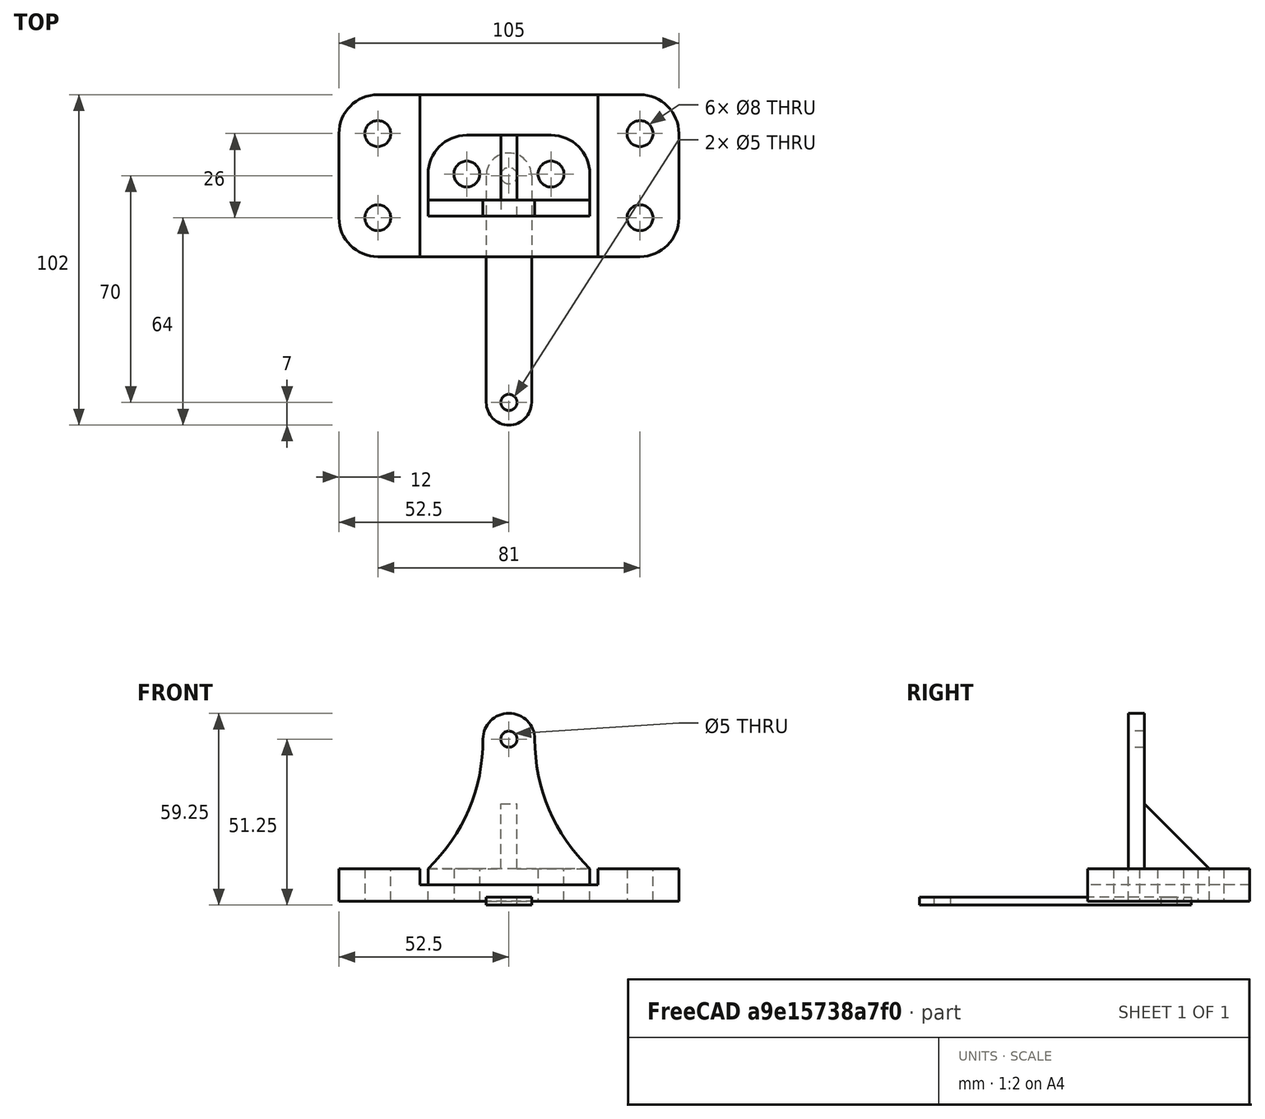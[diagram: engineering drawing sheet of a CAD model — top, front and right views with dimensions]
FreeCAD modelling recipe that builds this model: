
FCSTD DOCUMENT  (FreeCAD 1.0R39319 (Git))
Label: Assignment_7.1_Base
License: All rights reserved
LicenseURL: https://en.wikipedia.org/wiki/All_rights_reserved
objects: TechDraw::DrawViewDimension×15, Sketcher::SketchObject×7, PartDesign::Pad×5, TechDraw::DrawProjGroupItem×4, TechDraw::DrawViewAnnotation×4, PartDesign::Body×3, TechDraw::DrawViewBalloon×3, PartDesign::Pocket×1, TechDraw::DrawSVGTemplate×1, TechDraw::DrawProjGroup×1, TechDraw::DrawPage×1
note: 58 computed .brp shape members not serialized (recipe doc carries the construction recipe); baked Part::Feature solids carry a one-line shape summary decoded from their .brp

FEATURE [Sketcher::SketchObject] Sketch
  ArcFitTolerance = 1e-06
  AttachmentSupport = -> [XY_Plane]
  FullyConstrained = true
  MakeInternals = false
  MapMode = 5
  sketch-geometry (14):
    g0: LineSegment StartX=-52.5 StartY=13 StartZ=0 EndX=-52.5 EndY=-13 EndZ=0
    g1: LineSegment StartX=-40.5 StartY=-25 StartZ=0 EndX=40.5 EndY=-25 EndZ=0
    g2: LineSegment StartX=52.5 StartY=-13 StartZ=0 EndX=52.5 EndY=13 EndZ=0
    g3: LineSegment StartX=40.5 StartY=25 StartZ=0 EndX=-40.5 EndY=25 EndZ=0
    g4: ArcOfCircle CenterX=-40.5 CenterY=13 CenterZ=0 NormalX=0 NormalY=0 NormalZ=1 AngleXU=0 Radius=12 StartAngle=1.5708 EndAngle=3.14159
    g5: ArcOfCircle CenterX=-40.5 CenterY=-13 CenterZ=0 NormalX=0 NormalY=0 NormalZ=1 AngleXU=0 Radius=12 StartAngle=3.14159 EndAngle=4.71239
    g6: ArcOfCircle CenterX=40.5 CenterY=-13 CenterZ=0 NormalX=0 NormalY=0 NormalZ=1 AngleXU=0 Radius=12 StartAngle=4.71239 EndAngle=6.28319
    g7: ArcOfCircle CenterX=40.5 CenterY=13 CenterZ=0 NormalX=0 NormalY=0 NormalZ=1 AngleXU=0 Radius=12 StartAngle=0 EndAngle=1.5708
    g8: GeomPoint [constr] X=-52.5 Y=25 Z=0
    g9: GeomPoint [constr] X=52.5 Y=-25 Z=0
    g10: Circle CenterX=-40.5 CenterY=13 CenterZ=0 NormalX=0 NormalY=0 NormalZ=1 AngleXU=0 Radius=4
    g11: Circle CenterX=40.5 CenterY=13 CenterZ=0 NormalX=0 NormalY=0 NormalZ=1 AngleXU=0 Radius=4
    g12: Circle CenterX=40.5 CenterY=-13 CenterZ=0 NormalX=0 NormalY=0 NormalZ=1 AngleXU=0 Radius=4
    g13: Circle CenterX=-40.5 CenterY=-13 CenterZ=0 NormalX=0 NormalY=0 NormalZ=1 AngleXU=0 Radius=4
  constraints (31):
    c: Tangent(g0,g4) = -1.5708
    c: Tangent(g0,g5) = -1.5708
    c: Tangent(g1,g5) = -1.5708
    c: Tangent(g1,g6) = -1.5708
    c: Tangent(g2,g6) = -1.5708
    c: Tangent(g2,g7) = -1.5708
    c: Tangent(g3,g7) = -1.5708
    c: Tangent(g3,g4) = -1.5708
    c: Vertical(g0)
    c: Vertical(g2)
    c: Horizontal(g1)
    c: Horizontal(g3)
    c: Equal(g4,g5)
    c: Equal(g5,g6)
    c: Equal(g6,g7)
    c: PointOnObject(g8,g0)
    c: PointOnObject(g8,g3)
    c: PointOnObject(g9,g1)
    c: PointOnObject(g9,g2)
    c: Symmetric(g4,g6,g-1)
    c: Distance(g2,g0) = 105
    c: Distance(g1,g3) = 50
    c: Radius(g4) = 12
    c: Coincident(g10,g4)
    c: Coincident(g11,g7)
    c: Coincident(g12,g6)
    c: Coincident(g13,g5)
    c: Equal(g10,g11)
    c: Equal(g10,g12)
    c: Equal(g10,g13)
    c: Diameter(g10) = 8
FEATURE [PartDesign::Pad] Pad
  Direction = (0,0,1)
  Length = 10
  Length2 = 10
  Profile = -> Sketch
  ReferenceAxis = -> Sketch [N_Axis]
  Refine = true
  Suppressed = false
  Type = 0
FEATURE [Sketcher::SketchObject] Sketch001
  ArcFitTolerance = 1e-06
  AttachmentSupport = -> [Pad]
  ExternalGeometry = -> [Pad]
  FullyConstrained = true
  MakeInternals = false
  MapMode = 5
  Placement = pos=(0,0,10) rot=(0,0,1;0rad)
  sketch-geometry (5):
    g0: LineSegment StartX=27.5 StartY=-25 StartZ=0 EndX=27.5 EndY=25 EndZ=0
    g1: LineSegment StartX=27.5 StartY=25 StartZ=0 EndX=-27.5 EndY=25 EndZ=0
    g2: LineSegment StartX=-27.5 StartY=25 StartZ=0 EndX=-27.5 EndY=-25 EndZ=0
    g3: LineSegment StartX=-27.5 StartY=-25 StartZ=0 EndX=27.5 EndY=-25 EndZ=0
    g4: GeomPoint [constr] X=0 Y=0 Z=0
  constraints (12):
    c: Coincident(g0,g1)
    c: Coincident(g1,g2)
    c: Coincident(g2,g3)
    c: Coincident(g3,g0)
    c: Vertical(g0)
    c: Vertical(g2)
    c: Horizontal(g1)
    c: Horizontal(g3)
    c: Symmetric(g2,g0,g4)
    c: Coincident(g4,g-1)
    c: PointOnObject(g1,g-3)
    c: Distance(g0,g2) = 55
FEATURE [PartDesign::Pocket] Pocket
  BaseFeature = -> Pad
  Direction = (0,0,-1)
  Length = 5
  Length2 = 5
  Profile = -> Sketch001
  ReferenceAxis = -> Sketch001 [N_Axis]
  Refine = true
  Suppressed = false
  Type = 0
FEATURE [PartDesign::Body] Body  label="Base"
  AllowCompound = false
  Group = -> [Sketch,Pad,Sketch001,Pocket]
  Origin = -> Origin
  Tip = -> Pocket
FEATURE [Sketcher::SketchObject] Sketch002
  ArcFitTolerance = 1e-06
  AttachmentSupport = -> [XY_Plane001]
  FullyConstrained = true
  MakeInternals = false
  MapMode = 5
  sketch-geometry (11):
    g0: LineSegment StartX=-25 StartY=-12.5 StartZ=0 EndX=25 EndY=-12.5 EndZ=0
    g1: LineSegment StartX=25 StartY=-12.5 StartZ=0 EndX=25 EndY=0.5 EndZ=0
    g2: LineSegment StartX=13 StartY=12.5 StartZ=0 EndX=-13 EndY=12.5 EndZ=0
    g3: LineSegment StartX=-25 StartY=0.5 StartZ=0 EndX=-25 EndY=-12.5 EndZ=0
    g4: GeomPoint [constr] X=0 Y=0 Z=0
    g5: ArcOfCircle CenterX=-13 CenterY=0.5 CenterZ=0 NormalX=0 NormalY=0 NormalZ=1 AngleXU=0 Radius=12 StartAngle=1.5708 EndAngle=3.14159
    g6: GeomPoint [constr] X=-25 Y=12.5 Z=0
    g7: ArcOfCircle CenterX=13 CenterY=0.5 CenterZ=0 NormalX=0 NormalY=0 NormalZ=1 AngleXU=0 Radius=12 StartAngle=0 EndAngle=1.5708
    g8: GeomPoint [constr] X=25 Y=12.5 Z=0
    g9: Circle CenterX=13 CenterY=0.5 CenterZ=0 NormalX=0 NormalY=0 NormalZ=1 AngleXU=0 Radius=4
    g10: Circle CenterX=-13 CenterY=0.5 CenterZ=0 NormalX=0 NormalY=0 NormalZ=1 AngleXU=0 Radius=4
  constraints (24):
    c: Coincident(g0,g1)
    c: Coincident(g3,g0)
    c: Horizontal(g0)
    c: Horizontal(g2)
    c: Vertical(g1)
    c: Vertical(g3)
    c: Symmetric(g8,g0,g4)
    c: Distance(g1,g3) = 50
    c: Distance(g0,g6) = 25
    c: Coincident(g4,g-1)
    c: PointOnObject(g6,g3)
    c: PointOnObject(g6,g2)
    c: Tangent(g3,g5) = -1.5708
    c: Tangent(g2,g5) = -1.5708
    c: PointOnObject(g8,g1)
    c: PointOnObject(g8,g2)
    c: Tangent(g1,g7) = -1.5708
    c: Tangent(g2,g7) = -1.5708
    c: Equal(g5,g7)
    c: Radius(g5) = 12
    c: Coincident(g9,g7)
    c: Coincident(g10,g5)
    c: Equal(g10,g9)
    c: Diameter(g10) = 8
FEATURE [PartDesign::Pad] Pad001
  Direction = (0,0,1)
  Length = 10
  Length2 = 10
  Profile = -> Sketch002
  ReferenceAxis = -> Sketch002 [N_Axis]
  Refine = true
  Suppressed = false
  Type = 0
FEATURE [Sketcher::SketchObject] Sketch003
  ArcFitTolerance = 1e-06
  AttachmentSupport = -> [Pad001]
  FullyConstrained = true
  MakeInternals = false
  MapMode = 5
  Placement = pos=(0,-12.5,0) rot=(1,0,0;1.5708rad)
FEATURE [Sketcher::SketchObject] Sketch004
  ArcFitTolerance = 1e-06
  AttachmentSupport = -> [Pad001]
  ExternalGeometry = -> [Pad001]
  FullyConstrained = true
  MakeInternals = false
  MapMode = 5
  Placement = pos=(0,-12.5,0) rot=(1,0,0;1.5708rad)
  sketch-geometry (5):
    g0: ArcOfCircle CenterX=-63.5588 CenterY=50 CenterZ=0 NormalX=0 NormalY=0 NormalZ=1 AngleXU=0 Radius=55.5588 StartAngle=5.47944 EndAngle=6.28319
    g1: ArcOfCircle CenterX=0 CenterY=50 CenterZ=0 NormalX=0 NormalY=0 NormalZ=1 AngleXU=0 Radius=8 StartAngle=0 EndAngle=3.14159
    g2: ArcOfCircle CenterX=63.5588 CenterY=50 CenterZ=0 NormalX=0 NormalY=0 NormalZ=1 AngleXU=0 Radius=55.5588 StartAngle=3.14159 EndAngle=3.94533
    g3: Circle CenterX=0 CenterY=50 CenterZ=0 NormalX=0 NormalY=0 NormalZ=1 AngleXU=0 Radius=2.5
    g4: LineSegment StartX=-25 StartY=10 StartZ=0 EndX=25 EndY=10 EndZ=0
  constraints (13):
    c: Tangent(g0,g1) = 1.5708
    c: Tangent(g1,g2) = 1.5708
    c: Coincident(g2,g-4)
    c: Coincident(g0,g-5)
    c: PointOnObject(g1,g-2)
    c: Equal(g0,g2)
    c: Radius(g1) = 8
    c: Coincident(g3,g1)
    c: Diameter(g3) = 5
    c: Horizontal(g0,g1)
    c: DistanceY(g-1,g1) = 50
    c: Coincident(g4,g0)
    c: Coincident(g4,g2)
FEATURE [PartDesign::Pad] Pad002
  BaseFeature = -> Pad001
  Direction = (0,-1,2e-16)
  Length = 5
  Length2 = 10
  Profile = -> Sketch004
  ReferenceAxis = -> Sketch004 [N_Axis]
  Refine = true
  Reversed = true
  Suppressed = false
  Type = 0
FEATURE [Sketcher::SketchObject] Sketch008
  ArcFitTolerance = 1e-06
  AttachmentSupport = -> [YZ_Plane001]
  ExternalGeometry = -> [Pad002]
  FullyConstrained = true
  MakeInternals = false
  MapMode = 5
  Placement = pos=(0,0,0) rot=(0.57735,0.57735,0.57735;2.0944rad)
  sketch-geometry (3):
    g0: LineSegment StartX=-7.5 StartY=10 StartZ=0 EndX=-7.5 EndY=30 EndZ=0
    g1: LineSegment StartX=12.5 StartY=10 StartZ=0 EndX=-7.5 EndY=30 EndZ=0
    g2: LineSegment StartX=12.5 StartY=10 StartZ=0 EndX=-7.5 EndY=10 EndZ=0
  constraints (7):
    c: Coincident(g0,g-3)
    c: PointOnObject(g0,g-3)
    c: Coincident(g1,g-4)
    c: Coincident(g1,g0)
    c: Coincident(g2,g1)
    c: Coincident(g2,g0)
    c: DistanceY(g0,g0) = 20
FEATURE [PartDesign::Pad] Pad004
  BaseFeature = -> Pad002
  Direction = (1,0,0)
  Length = 5
  Length2 = 10
  Midplane = true
  Profile = -> Sketch008
  ReferenceAxis = -> Sketch008 [N_Axis]
  Refine = true
  Suppressed = false
  Type = 0
FEATURE [PartDesign::Body] Body001  label="Bracket"
  AllowCompound = false
  Group = -> [Sketch002,Pad001,Sketch003,Sketch004,Pad002,Sketch008,Pad004]
  Origin = -> Origin001
  Tip = -> Pad004
FEATURE [Sketcher::SketchObject] Sketch009
  ArcFitTolerance = 1e-06
  AttachmentSupport = -> [XY_Plane002]
  FullyConstrained = true
  MakeInternals = false
  MapMode = 5
  sketch-geometry (6):
    g0: ArcOfCircle CenterX=0 CenterY=0 CenterZ=0 NormalX=0 NormalY=0 NormalZ=1 AngleXU=0 Radius=7 StartAngle=1e-16 EndAngle=3.14159
    g1: ArcOfCircle CenterX=2e-16 CenterY=-70 CenterZ=0 NormalX=0 NormalY=0 NormalZ=1 AngleXU=0 Radius=7 StartAngle=3.14159 EndAngle=6.28319
    g2: LineSegment StartX=7 StartY=9e-16 StartZ=0 EndX=7 EndY=-70 EndZ=0
    g3: LineSegment StartX=-7 StartY=0 StartZ=0 EndX=-7 EndY=-70 EndZ=0
    g4: Circle CenterX=0 CenterY=0 CenterZ=0 NormalX=0 NormalY=0 NormalZ=1 AngleXU=0 Radius=2.5
    g5: Circle CenterX=2e-16 CenterY=-70 CenterZ=0 NormalX=0 NormalY=0 NormalZ=1 AngleXU=0 Radius=2.5
  constraints (13):
    c: Tangent(g0,g2) = 1.5708
    c: Tangent(g0,g3) = -1.5708
    c: Tangent(g1,g2) = 1.5708
    c: Tangent(g1,g3) = -1.5708
    c: Equal(g0,g1)
    c: Vertical(g3)
    c: Coincident(g0,g-1)
    c: Coincident(g5,g1)
    c: Equal(g4,g5)
    c: Diameter(g4) = 5
    c: DistanceY(g1,g4) = 70
    c: Coincident(g0,g4)
    c: Radius(g0) = 7
FEATURE [PartDesign::Pad] Pad005
  Direction = (0,0,1)
  Length = 2.5
  Length2 = 10
  Midplane = true
  Profile = -> Sketch009
  ReferenceAxis = -> Sketch009 [N_Axis]
  Refine = true
  Suppressed = false
  Type = 0
FEATURE [PartDesign::Body] Body002  label="Links"
  AllowCompound = false
  Group = -> [Sketch009,Pad005]
  Origin = -> Origin002
  Tip = -> Pad005
FEATURE [TechDraw::DrawSVGTemplate] Template002
  EditableTexts = AuthorName=REHAN K. NADAF; CheckDate=CHECK DATE; CreationDate=29-11-2025; DrawingNumber=NUMBER; FC-Title=Bracket; SheetNumber=3 / 3; Subtitle=Assignment_7.1_Slider_Assembly; SupervisorName=ProBUILD; Weight=WEIGHT; scale=1 : 1
  Height = 297
  Orientation = 1
  Template = C:/Program Files/FreeCAD 1.0/data/Mod/TechDraw/Templates/A3_Landscape_TD.svg
  Width = 420
FEATURE [TechDraw::DrawProjGroupItem] View001  label="Front001"
  CoarseView = false
  Direction = (2e-16,1,0)
  Focus = 100
  HardHidden = true
  IsoCount = 0
  IsoHidden = false
  IsoVisible = false
  LockPosition = true
  Perspective = false
  Rotation = 0
  RotationVector = (1,0,0)
  Scale = 1.5
  ScaleType = 2
  ScrubCount = 1
  SeamHidden = false
  SeamVisible = false
  SmoothHidden = false
  SmoothVisible = true
  Source = -> [Body001]
  Type = 0
  X = 0
  XDirection = (-1,2e-16,0)
  Y = 0
FEATURE [TechDraw::DrawProjGroupItem] ProjItem002  label="Left"
  CoarseView = false
  Direction = (1,-1e-16,0)
  Focus = 100
  HardHidden = true
  IsoCount = 0
  IsoHidden = false
  IsoVisible = false
  LockPosition = false
  Perspective = false
  Rotation = 0
  RotationVector = (1,0,0)
  Scale = 1.5
  ScaleType = 2
  ScrubCount = 1
  SeamHidden = false
  SeamVisible = false
  SmoothHidden = false
  SmoothVisible = true
  Source = -> [Body001]
  Type = 1
  X = -161.206
  XDirection = (1e-16,1,0)
  Y = 0
FEATURE [TechDraw::DrawProjGroupItem] ProjItem  label="FrontTopRight"
  CoarseView = true
  Direction = (-0.57735,0.57735,0.57735)
  Focus = 100
  HardHidden = false
  IsoCount = 0
  IsoHidden = true
  IsoVisible = false
  LockPosition = true
  Perspective = false
  Rotation = 0
  RotationVector = (1,0,0)
  Scale = 1.5
  ScaleType = 2
  ScrubCount = 1
  SeamHidden = false
  SeamVisible = false
  SmoothHidden = false
  SmoothVisible = true
  Source = -> [Body001]
  Type = 7
  X = -271.118
  XDirection = (-0.707107,-0.707107,0)
  Y = 105.092
FEATURE [TechDraw::DrawViewDimension] Dimension
  AngleOverride = false
  Arbitrary = false
  ArbitraryTolerances = false
  BoxCorners = (2) [(-12.5,-29,-1e-07),(12.5,29,1e-07)]
  EqualTolerance = true
  ExtensionAngle = 0
  FormatSpec = %.2w
  FormatSpecOverTolerance = %+.2w
  FormatSpecUnderTolerance = %+.2w
  Inverted = false
  LineAngle = 0
  LockPosition = false
  MeasureType = 1
  OverTolerance = 0
  References2D = -> [ProjItem002]
  Rotation = 0
  ScaleType = 0
  TheoreticalExact = false
  Type = 0
  UnderTolerance = 0
  X = 22.1548
  Y = -11.0669
FEATURE [TechDraw::DrawViewDimension] Dimension004
  AngleOverride = false
  Arbitrary = false
  ArbitraryTolerances = false
  BoxCorners = (2) [(-25,-29,-1e-07),(25,29,1e-07)]
  EqualTolerance = true
  ExtensionAngle = 0
  FormatSpec = R%.2w
  FormatSpecOverTolerance = %+.2w
  FormatSpecUnderTolerance = %+.2w
  Inverted = false
  LineAngle = 0
  LockPosition = false
  MeasureType = 1
  OverTolerance = 0
  References2D = -> [View001]
  Rotation = 0
  ScaleType = 0
  TheoreticalExact = false
  Type = 4
  UnderTolerance = 0
  X = 33.9135
  Y = 48.0796
FEATURE [TechDraw::DrawViewDimension] Dimension005
  AngleOverride = false
  Arbitrary = false
  ArbitraryTolerances = false
  BoxCorners = (2) [(-25,-29,-1e-07),(25,29,1e-07)]
  EqualTolerance = true
  ExtensionAngle = 0
  FormatSpec = ⌀%.2w
  FormatSpecOverTolerance = %+.2w
  FormatSpecUnderTolerance = %+.2w
  Inverted = false
  LineAngle = 0
  LockPosition = false
  MeasureType = 1
  OverTolerance = 0
  References2D = -> [View001]
  Rotation = 0
  ScaleType = 0
  TheoreticalExact = false
  Type = 5
  UnderTolerance = 0
  X = 37.2148
  Y = 31.4331
FEATURE [TechDraw::DrawViewDimension] Dimension006
  AngleOverride = false
  Arbitrary = false
  ArbitraryTolerances = false
  BoxCorners = (2) [(-25,-29,-1e-07),(25,29,1e-07)]
  EqualTolerance = true
  ExtensionAngle = 0
  FormatSpec = R%.2w
  FormatSpecOverTolerance = %+.2w
  FormatSpecUnderTolerance = %+.2w
  Inverted = false
  LineAngle = 0
  LockPosition = false
  MeasureType = 1
  OverTolerance = 0
  References2D = -> [View001]
  Rotation = 0
  ScaleType = 0
  TheoreticalExact = false
  Type = 4
  UnderTolerance = 0
  X = -54.0533
  Y = 26.8958
FEATURE [TechDraw::DrawViewDimension] Dimension007
  AngleOverride = false
  Arbitrary = false
  ArbitraryTolerances = false
  BoxCorners = (2) [(-25,-29,-1e-07),(25,29,1e-07)]
  EqualTolerance = true
  ExtensionAngle = 0
  FormatSpec = %.2w
  FormatSpecOverTolerance = %+.2w
  FormatSpecUnderTolerance = %+.2w
  Inverted = false
  LineAngle = 0
  LockPosition = false
  MeasureType = 1
  OverTolerance = 0
  References2D = -> [View001]
  Rotation = 0
  ScaleType = 0
  TheoreticalExact = false
  Type = 0
  UnderTolerance = 0
  X = 57.0338
  Y = -13.5
FEATURE [TechDraw::DrawViewDimension] Dimension008
  AngleOverride = false
  Arbitrary = false
  ArbitraryTolerances = false
  BoxCorners = (2) [(-25,-29,-1e-07),(25,29,1e-07)]
  EqualTolerance = true
  ExtensionAngle = 0
  FormatSpec = %.2w
  FormatSpecOverTolerance = %+.2w
  FormatSpecUnderTolerance = %+.2w
  Inverted = false
  LineAngle = 0
  LockPosition = false
  MeasureType = 1
  OverTolerance = 0
  References2D = -> [View001]
  Rotation = 0
  ScaleType = 0
  TheoreticalExact = false
  Type = 0
  UnderTolerance = 0
  X = -45.6785
  Y = -2.57298
FEATURE [TechDraw::DrawViewDimension] Dimension002
  AngleOverride = false
  Arbitrary = false
  ArbitraryTolerances = false
  BoxCorners = (2) [(-12.5,-29,0),(12.5,29,0)]
  EqualTolerance = true
  ExtensionAngle = 0
  FormatSpec = %.2w
  FormatSpecOverTolerance = %+.2w
  FormatSpecUnderTolerance = %+.2w
  Inverted = false
  LineAngle = 0
  LockPosition = false
  MeasureType = 1
  OverTolerance = 0
  References2D = -> [ProjItem002]
  Rotation = 0
  ScaleType = 0
  TheoreticalExact = false
  Type = 0
  UnderTolerance = 0
  X = -31.1479
  Y = 68.497
FEATURE [TechDraw::DrawViewDimension] Dimension003
  AngleOverride = false
  Arbitrary = false
  ArbitraryTolerances = false
  BoxCorners = (2) [(-12.5,-29,0),(12.5,29,0)]
  EqualTolerance = true
  ExtensionAngle = 0
  FormatSpec = %.2w
  FormatSpecOverTolerance = %+.2w
  FormatSpecUnderTolerance = %+.2w
  Inverted = false
  LineAngle = 0
  LockPosition = false
  MeasureType = 1
  OverTolerance = 0
  References2D = -> [ProjItem002]
  Rotation = 0
  ScaleType = 0
  TheoreticalExact = false
  Type = 0
  UnderTolerance = 0
  X = -37.5591
  Y = 0
FEATURE [TechDraw::DrawViewBalloon] Balloon
  BubbleShape = 5
  EndType = 0
  EndTypeScale = 1
  KinkLength = 5
  LockPosition = false
  OriginX = -2.9981
  OriginY = 28.5792
  Rotation = 0
  ScaleType = 0
  ShapeScale = 1
  SourceView = -> View001
  Text = 1
  TextWrapLen = -1
  X = -28.629
  Y = 37.8066
FEATURE [TechDraw::DrawViewBalloon] Balloon001
  BubbleShape = 5
  EndType = 0
  EndTypeScale = 1
  KinkLength = 5
  LockPosition = false
  OriginX = -9.86482
  OriginY = 28.8382
  Rotation = 0
  ScaleType = 0
  ShapeScale = 1
  SourceView = -> ProjItem002
  Text = 2
  TextWrapLen = -1
  X = 9.09844
  Y = 39.7639
FEATURE [TechDraw::DrawProjGroupItem] ProjItem003  label="Top"
  CoarseView = false
  Direction = (0,0,1)
  Focus = 100
  HardHidden = true
  IsoCount = 0
  IsoHidden = false
  IsoVisible = false
  LockPosition = false
  Perspective = false
  Rotation = 0
  RotationVector = (1,0,0)
  Scale = 1.5
  ScaleType = 2
  ScrubCount = 1
  SeamHidden = false
  SeamVisible = false
  SmoothHidden = true
  SmoothVisible = true
  Source = -> [Body001]
  Type = 4
  X = 0
  XDirection = (-1,2e-16,0)
  Y = 99.8263
FEATURE [TechDraw::DrawProjGroup] ProjGroup004
  Anchor = -> View001
  AutoDistribute = false
  LockPosition = false
  ProjectionType = 1
  Rotation = 0
  Scale = 1.5
  ScaleType = 1
  Source = -> [Body001]
  Views = -> [View001,ProjItem002,ProjItem,ProjItem003]
  X = 321.881
  Y = 130.081
  spacingX = 20
  spacingY = 20
FEATURE [TechDraw::DrawViewDimension] Dimension016
  AngleOverride = false
  Arbitrary = false
  ArbitraryTolerances = false
  BoxCorners = (2) [(-25,-12.5,-1e-07),(25,12.5,1e-07)]
  EqualTolerance = true
  ExtensionAngle = 0
  FormatSpec = %.2w
  FormatSpecOverTolerance = %+.2w
  FormatSpecUnderTolerance = %+.2w
  Inverted = false
  LineAngle = 0
  LockPosition = false
  MeasureType = 1
  OverTolerance = 0
  References2D = -> [ProjItem003]
  Rotation = 0
  ScaleType = 0
  TheoreticalExact = false
  Type = 0
  UnderTolerance = 0
  X = 3.154
  Y = 45.9061
FEATURE [TechDraw::DrawViewDimension] Dimension017
  AngleOverride = false
  Arbitrary = false
  ArbitraryTolerances = false
  BoxCorners = (2) [(-25,-12.5,-1e-07),(25,12.5,1e-07)]
  EqualTolerance = true
  ExtensionAngle = 0
  FormatSpec = ⌀%.2w
  FormatSpecOverTolerance = %+.2w
  FormatSpecUnderTolerance = %+.2w
  Inverted = false
  LineAngle = 0
  LockPosition = false
  MeasureType = 1
  OverTolerance = 0
  References2D = -> [ProjItem003]
  Rotation = 0
  ScaleType = 0
  TheoreticalExact = false
  Type = 5
  UnderTolerance = 0
  X = -52.6199
  Y = -17.6047
FEATURE [TechDraw::DrawViewDimension] Dimension018
  AngleOverride = false
  Arbitrary = false
  ArbitraryTolerances = false
  BoxCorners = (2) [(-25,-12.5,-1e-07),(25,12.5,1e-07)]
  EqualTolerance = true
  ExtensionAngle = 0
  FormatSpec = %.2w
  FormatSpecOverTolerance = %+.2w
  FormatSpecUnderTolerance = %+.2w
  Inverted = false
  LineAngle = 0
  LockPosition = false
  MeasureType = 1
  OverTolerance = 0
  References2D = -> [ProjItem003]
  Rotation = 0
  ScaleType = 0
  TheoreticalExact = false
  Type = 1
  UnderTolerance = 0
  X = 0
  Y = 33.6793
FEATURE [TechDraw::DrawViewDimension] Dimension019
  AngleOverride = false
  Arbitrary = false
  ArbitraryTolerances = false
  BoxCorners = (2) [(-25,-12.5,-1e-07),(25,12.5,1e-07)]
  EqualTolerance = true
  ExtensionAngle = 0
  FormatSpec = R%.2w
  FormatSpecOverTolerance = %+.2w
  FormatSpecUnderTolerance = %+.2w
  Inverted = false
  LineAngle = 0
  LockPosition = false
  MeasureType = 1
  OverTolerance = 0
  References2D = -> [ProjItem003]
  Rotation = 0
  ScaleType = 0
  TheoreticalExact = false
  Type = 4
  UnderTolerance = 0
  X = 66.3656
  Y = -15.7593
FEATURE [TechDraw::DrawViewDimension] Dimension020
  AngleOverride = false
  Arbitrary = false
  ArbitraryTolerances = false
  BoxCorners = (2) [(-25,-12.5,-1e-07),(25,12.5,1e-07)]
  EqualTolerance = true
  ExtensionAngle = 0
  FormatSpec = %.2w
  FormatSpecOverTolerance = %+.2w
  FormatSpecUnderTolerance = %+.2w
  Inverted = false
  LineAngle = 0
  LockPosition = false
  MeasureType = 1
  OverTolerance = 0
  References2D = -> [ProjItem003]
  Rotation = 0
  ScaleType = 0
  TheoreticalExact = false
  Type = 0
  UnderTolerance = 0
  X = -72.5268
  Y = 9
FEATURE [TechDraw::DrawViewDimension] Dimension021
  AngleOverride = false
  Arbitrary = false
  ArbitraryTolerances = false
  BoxCorners = (2) [(-25,-12.5,-1e-07),(25,12.5,1e-07)]
  EqualTolerance = true
  ExtensionAngle = 0
  FormatSpec = %.2w
  FormatSpecOverTolerance = %+.2w
  FormatSpecUnderTolerance = %+.2w
  Inverted = false
  LineAngle = 0
  LockPosition = false
  MeasureType = 1
  OverTolerance = 0
  References2D = -> [ProjItem003]
  Rotation = 0
  ScaleType = 0
  TheoreticalExact = false
  Type = 0
  UnderTolerance = 0
  X = 64.8298
  Y = 9.18968
FEATURE [TechDraw::DrawViewBalloon] Balloon002
  BubbleShape = 5
  EndType = 0
  EndTypeScale = 1
  KinkLength = 5
  LockPosition = false
  OriginX = -18.3998
  OriginY = 12.6069
  Rotation = 0
  ScaleType = 0
  ShapeScale = 1
  SourceView = -> ProjItem003
  Text = 3
  TextWrapLen = -1
  X = -42.2149
  Y = 26.7125
FEATURE [TechDraw::DrawViewAnnotation] Annotation  label="Front View"
  Font = osifont
  LineSpace = 100
  LockPosition = false
  MaxWidth = -1
  Rotation = 0
  ScaleType = 0
  Text = Front View
  TextSize = 5
  TextStyle = 0
  X = 321.881
  Y = 78.914
FEATURE [TechDraw::DrawViewAnnotation] Annotation001
  Font = osifont
  LineSpace = 100
  LockPosition = false
  MaxWidth = -1
  Rotation = 0
  ScaleType = 0
  Text = Side View
  TextSize = 5
  TextStyle = 0
  X = 160.675
  Y = 64.988
FEATURE [TechDraw::DrawViewAnnotation] Annotation002
  Font = osifont
  LineSpace = 100
  LockPosition = false
  MaxWidth = -1
  Rotation = 0
  ScaleType = 0
  Text = Top View
  TextSize = 5
  TextStyle = 0
  X = 321.881
  Y = 203.124
FEATURE [TechDraw::DrawViewAnnotation] Annotation003
  Font = osifont
  LineSpace = 100
  LockPosition = false
  MaxWidth = -1
  Rotation = 0
  ScaleType = 0
  Text = Isometric View
  TextSize = 5
  TextStyle = 0
  X = 50.7631
  Y = 179.056
FEATURE [TechDraw::DrawViewDimension] Dimension022
  AngleOverride = false
  Arbitrary = false
  ArbitraryTolerances = false
  BoxCorners = (2) [(-18.75,-43.5,-1e-07),(18.75,43.5,1e-07)]
  EqualTolerance = true
  ExtensionAngle = 0
  FormatSpec = %.2w
  FormatSpecOverTolerance = %+.2w
  FormatSpecUnderTolerance = %+.2w
  Inverted = false
  LineAngle = 0
  LockPosition = false
  MeasureType = 1
  OverTolerance = 0
  References2D = -> [ProjItem002]
  Rotation = 0
  ScaleType = 0
  TheoreticalExact = false
  Type = 0
  UnderTolerance = 0
  X = 0
  Y = -46.9175
FEATURE [TechDraw::DrawPage] Page002  label="Bracket Drawing"
  KeepUpdated = true
  NextBalloonIndex = 6
  ProjectionType = 0
  Template = -> Template002
  Views = -> [ProjGroup004,Dimension,Dimension002,Dimension003,Dimension004,Dimension005,Dimension006,Dimension007,Dimension008,Balloon,Balloon001,Dimension016,Dimension017,Dimension018,Dimension019,Dimension020,Dimension021,Balloon002,Annotation,Annotation001,Annotation002,Annotation003,Dimension022]
